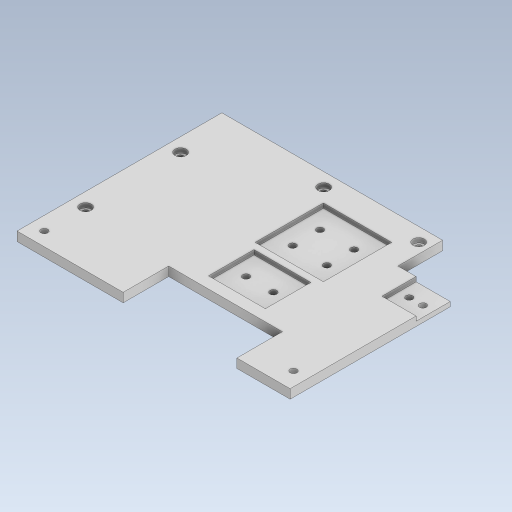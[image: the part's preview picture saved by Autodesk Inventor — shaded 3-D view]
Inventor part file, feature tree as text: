
AUTODESK INVENTOR PART (.ipt)
format: ipt  version: 2023.5 (Build 275446000, 446)  size: 174,080 bytes
history: native  units: in
note: dims shown in document units (in); Inventor stores cm internally (conversion verified against a paired STEP export)
features: extrude x2, sketch x1
ambient origin geometry x8: Origin, YZ Plane, XZ Plane, XY Plane, X Axis, Y Axis, Z Axis, Center Point
bodies: Solid1 (feature_tree)
feature tree (3):
  sketch  "Sketch1"  dims[d28=0.1575in d29=0.0in d30=0.0787in d31=0.0in d32=0.2953in d33=0.4724in d34=0.4724in d35=0.2953in d36=0.0in d37=0.0in d39=0.315in]
  extrude  "Extrusion1"  Depth=0.0787in TaperAngle=0.0deg
  extrude  "Extrusion2"  Depth=0.315in
